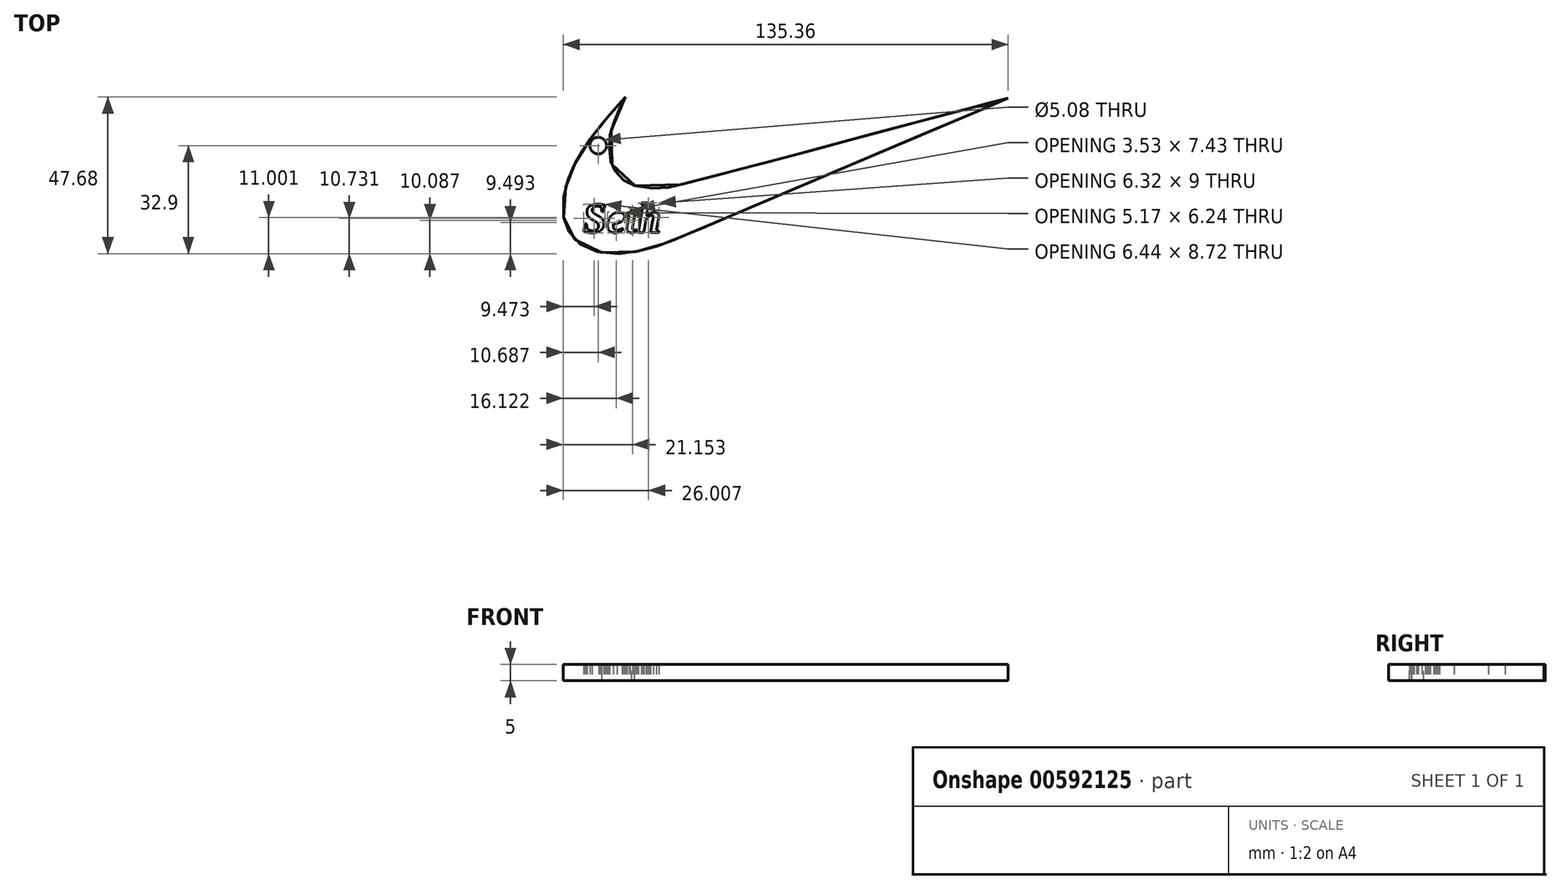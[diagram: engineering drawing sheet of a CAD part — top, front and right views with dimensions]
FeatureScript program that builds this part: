
annotation { "Feature Type Name" : "Feature", "Feature Type Description" : "" }
export const myFeature = defineFeature(function(context is Context, id is Id, definition is map)
    precondition{}
    {
        {
            var Q0;
            Q0=qCreatedBy(makeId("Top.planeOp"),FACE);
            var sketch = newSketch(context, id + "F0", { "sketchPlane" : qUnion([Q0])});
            skFitSpline(sketch, "E0", {"points": [v(-47.07, 41.18) * mm, v(-47.75, 40.4) * mm, v(-48.57, 39.49) * mm, v(-49.12, 38.88) * mm, v(-50.03, 37.9) * mm, v(-50.85, 36.98) * mm, v(-52.07, 35.54) * mm, v(-53.31, 34.1) * mm, v(-54.32, 32.9) * mm, v(-55.09, 31.94) * mm, v(-56.03, 30.82) * mm, v(-56.88, 29.67) * mm, v(-57.52, 28.8) * mm, v(-58.34, 27.67) * mm, v(-59.22, 26.39) * mm, v(-59.94, 25.3) * mm, v(-60.8, 23.97) * mm, v(-61.43, 22.88) * mm, v(-61.92, 21.93) * mm, v(-62.69, 20.52) * mm, v(-63.29, 19.28) * mm, v(-63.64, 18.42) * mm, v(-64.04, 17.44) * mm, v(-64.42, 16.4) * mm, v(-64.77, 15.38) * mm, v(-65.18, 14.12) * mm, v(-65.55, 12.9) * mm, v(-65.78, 11.6) * mm, v(-65.93, 10.18) * mm, v(-66.06, 8.4) * mm, v(-66.06, 5.62) * mm, v(-65.93, 4.45) * mm, v(-65.76, 3.5) * mm, v(-65.47, 2.5) * mm, v(-64.98, 1.37) * mm, v(-64.45, 0.41) * mm, v(-63.76, -0.6) * mm, v(-62.85, -1.8) * mm, v(-62.18, -2.45) * mm, v(-61.14, -3.35) * mm, v(-59.89, -4.23) * mm, v(-58.26, -5.06) * mm, v(-56.66, -5.62) * mm, v(-54.97, -6.08) * mm, v(-53.35, -6.37) * mm, v(-51.85, -6.48) * mm, v(-48.75, -6.45) * mm, v(-46.6, -6.21) * mm, v(-44.56, -5.97) * mm, v(-43.1, -5.65) * mm, v(-41.79, -5.33) * mm, v(-40.5, -5.04) * mm, v(-39.09, -4.6) * mm, v(-37.25, -4.07) * mm, v(-35.78, -3.62) * mm, v(-34.92, -3.27) * mm, v(-33.62, -2.78) * mm, v(-32.6, -2.39) * mm, v(-31.46, -1.96) * mm, v(-30.78, -1.66) * mm, v(-29.78, -1.26) * mm, v(-29, -0.91) * mm, v(-27.23, -0.13) * mm, v(-26.2, 0.3) * mm, v(-24.78, 0.88) * mm, v(-23.67, 1.34) * mm, v(-22.83, 1.66) * mm, v(-21.29, 2.36) * mm, v(-13.65, 5.55) * mm, v(11.05, 16.16) * mm, v(31.34, 24.78) * mm, v(51.92, 33.42) * mm, v(61.69, 37.54) * mm, v(66.6, 39.62) * mm, v(69.27, 40.8) * mm, v(66.44, 40.15) * mm, v(59.55, 38.34) * mm, v(50.42, 35.88) * mm, v(25.06, 29.2) * mm, v(11.29, 25.47) * mm, v(1.51, 22.85) * mm, v(-9.32, 20.02) * mm, v(-14.78, 18.63) * mm, v(-21.09, 16.93) * mm, v(-23.93, 16.17) * mm, v(-26.63, 15.41) * mm, v(-29.6, 14.68) * mm, v(-33.97, 13.71) * mm, v(-36.47, 13.54) * mm, v(-40.71, 13.5) * mm, v(-44.36, 14.22) * mm, v(-46.47, 15.1) * mm, v(-47.79, 16) * mm, v(-49.36, 17.65) * mm, v(-50.5, 19.18) * mm, v(-51.05, 20.4) * mm, v(-51.47, 21.47) * mm, v(-51.94, 23.29) * mm, v(-51.98, 25.36) * mm, v(-52.03, 27.86) * mm, v(-51.53, 30.6) * mm, v(-50.89, 32.42) * mm, v(-49.96, 35.2) * mm, v(-48.93, 37.52) * mm, v(-47.65, 40.08) * mm, v(-47.07, 41.18) * mm]});
            skText(sketch, "E1", { "text": "Seth", "fontName": "Tinos-BoldItalic.ttf"});
            skCircle(sketch, "E2", {"center": v(-55.4, 26.4) * mm, "radius": 2.54 * mm});
            const initialGuessF0  = {"E1": [-0.06007, 0, 1, 0, 0.00934]};
            skSetInitialGuess(sketch, initialGuessF0);
            skSolve(sketch);
        }
        {
            var Q0;
            Q0=makeQuery(id+"F0.imprint","IMPRINT",FACE,{"disambiguationData":[TD([[makeQuery(id+"F0.imprint","IMPRINT",EDGE,{"derivedFrom":sQuery(id+"F0.wireOp",EDGE,"E0")}),1.0]])]});
            extrude(context, id + "F1", {"entities" : qUnion([Q0]), "depth" : 5 * mm, "offsetDistance" : 25 * mm});
        }
        {
            var Q0;
            Q0=sQuery(id+"F0.wireOp",EDGE,"E2");
            extrude(context, id + "F2", {"bodyType" : ToolBodyType.SURFACE, "surfaceEntities" : qUnion([Q0]), "depth" : 5 * mm, "offsetDistance" : 25 * mm});
        }
    });
